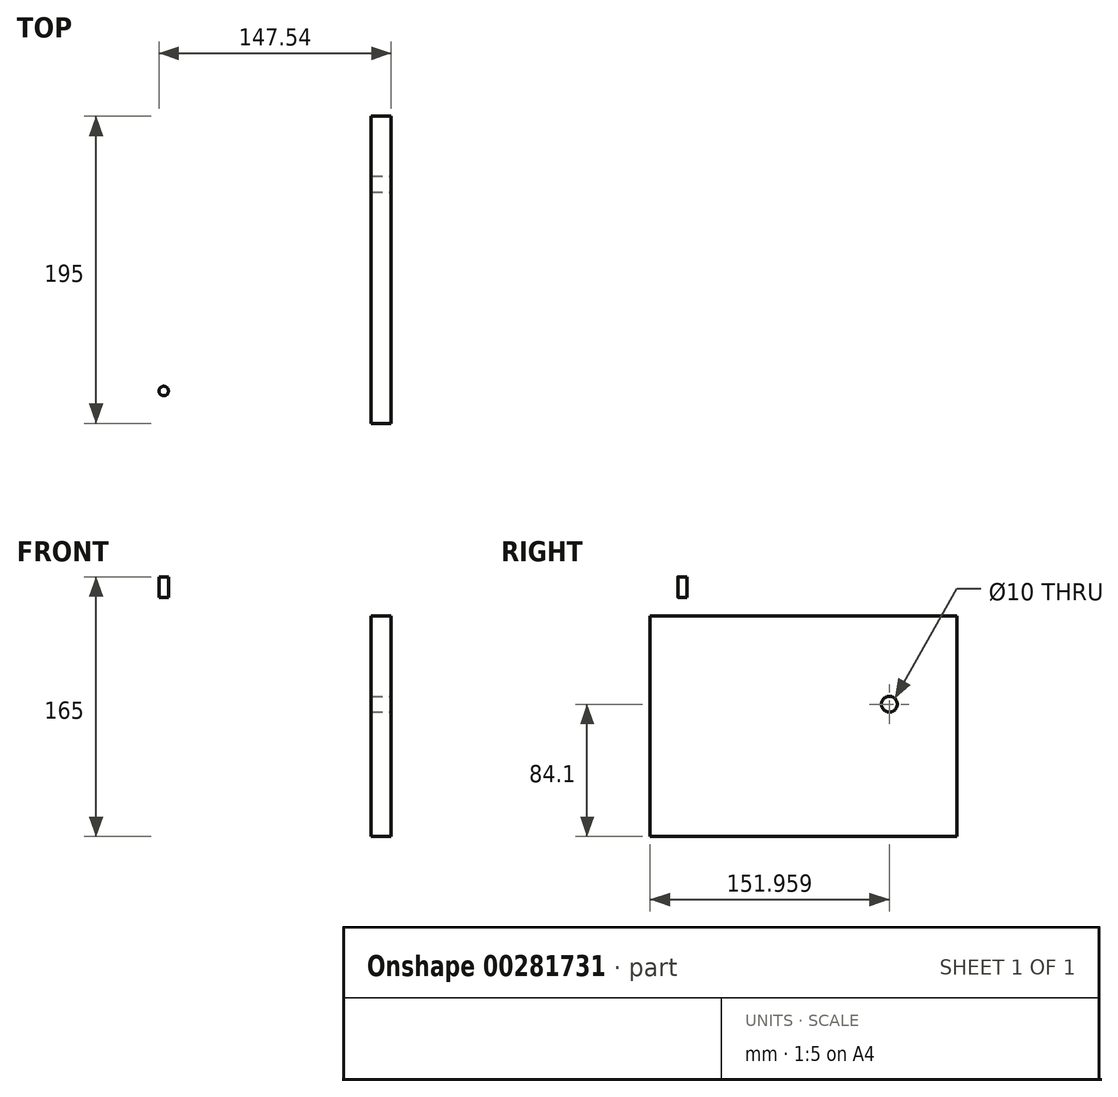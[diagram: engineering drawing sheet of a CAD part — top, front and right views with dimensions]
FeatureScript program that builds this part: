
annotation { "Feature Type Name" : "Feature", "Feature Type Description" : "" }
export const myFeature = defineFeature(function(context is Context, id is Id, definition is map)
    precondition{}
    {
        {
            var Q0;
            Q0=qCreatedBy(makeId("Front.planeOp"),FACE);
            var sketch = newSketch(context, id + "F0", { "sketchPlane" : qUnion([Q0])});
            skLineSegment(sketch, "E0", {"start": v(-1.16, 80.9) * mm, "end": v(-1.16, -84.1) * mm});
            skLineSegment(sketch, "E1", {"start": v(-1.16, -84.1) * mm, "end": v(-14.16, -84.1) * mm});
            skLineSegment(sketch, "E2", {"start": v(-14.16, -84.1) * mm, "end": v(-14.16, 57.9) * mm});
            skLineSegment(sketch, "E3", {"start": v(-24.16, 67.9) * mm, "end": v(-166.16, 67.9) * mm});
            skLineSegment(sketch, "E4", {"start": v(-166.16, 67.9) * mm, "end": v(-166.16, 80.9) * mm});
            skLineSegment(sketch, "E5", {"start": v(-166.16, 80.9) * mm, "end": v(-1.16, 80.9) * mm});
            skPoint(sketch, "E6.visualSharp", {"position": v(-14.16, 67.9) * mm});
            skArc(sketch, "E6.filletArc", {"start": v(-14.16, 57.9) * mm, "mid": v(-17.09, 64.97) * mm, "end": v(-24.16, 67.9) * mm});
            skSolve(sketch);
        }
        {
            var Q0;
            Q0=makeQuery(id+"F0.imprint","IMPRINT",FACE,{"disambiguationData":[TD([[makeQuery(id+"F0.imprint","IMPRINT",EDGE,{"derivedFrom":sQuery(id+"F0.wireOp",EDGE,"E0")}),-1.0]])]});
            extrude(context, id + "F1", {"entities" : qUnion([Q0]), "depth" : 195 * mm});
        }
        {
            var Q0;
            Q0=makeQuery(id+"F1.opExtrude","SWEPT_FACE",FACE,{"disambiguationData":[OSD([sQuery(id+"F0.wireOp",EDGE,"E5")])]});
            var sketch = newSketch(context, id + "F2", { "sketchPlane" : qUnion([Q0])});
            skCircle(sketch, "E7.MirrorC", {"center": v(-145.7, -174.46) * mm, "radius": 3 * mm});
            skArc(sketch, "E8.MirrorCS", {"start": v(-49.52, -16.1) * mm, "mid": v(-53.64, -17.1) * mm, "end": v(-52.63, -21.23) * mm});
            skArc(sketch, "E9.MirrorCS", {"start": v(-49.52, -16.1) * mm, "mid": v(-53.64, -17.1) * mm, "end": v(-52.63, -21.23) * mm, "construction": true});
            skArc(sketch, "E10.MirrorCS", {"start": v(-42.17, -28.1) * mm, "mid": v(-38, -27.38) * mm, "end": v(-38.7, -23.2) * mm});
            skArc(sketch, "E11.MirrorCS", {"start": v(-52.63, -21.23) * mm, "mid": v(-47.34, -24.57) * mm, "end": v(-42.17, -28.1) * mm});
            skArc(sketch, "E12.MirrorCS", {"start": v(-52.63, -21.23) * mm, "mid": v(-47.34, -24.57) * mm, "end": v(-42.17, -28.1) * mm, "construction": true});
            skArc(sketch, "E13.MirrorCS", {"start": v(-42.17, -28.1) * mm, "mid": v(-38, -27.38) * mm, "end": v(-38.7, -23.2) * mm, "construction": true});
            skArc(sketch, "E14.MirrorCS", {"start": v(-51.08, -18.67) * mm, "mid": v(-45.7, -22.06) * mm, "end": v(-40.44, -25.65) * mm, "construction": true});
            skArc(sketch, "E15.MirrorCS", {"start": v(-49.52, -16.1) * mm, "mid": v(-44.05, -19.56) * mm, "end": v(-38.7, -23.2) * mm});
            skArc(sketch, "E16.MirrorCS", {"start": v(-49.52, -16.1) * mm, "mid": v(-44.05, -19.56) * mm, "end": v(-38.7, -23.2) * mm, "construction": true});
            skArc(sketch, "E17.MirrorCS", {"start": v(-140.48, -25.15) * mm, "mid": v(-137.38, -22.26) * mm, "end": v(-140.27, -19.16) * mm});
            skArc(sketch, "E18.MirrorCS", {"start": v(-151.12, -19.16) * mm, "mid": v(-154.01, -22.26) * mm, "end": v(-150.91, -25.15) * mm});
            skArc(sketch, "E19.MirrorCS", {"start": v(-151.02, -22.16) * mm, "mid": v(-145.7, -22.06) * mm, "end": v(-140.38, -22.16) * mm, "construction": true});
            skArc(sketch, "E20.MirrorCS", {"start": v(-150.91, -25.15) * mm, "mid": v(-145.7, -25.06) * mm, "end": v(-140.48, -25.15) * mm});
            skArc(sketch, "E21.MirrorCS", {"start": v(-151.12, -19.16) * mm, "mid": v(-145.7, -19.06) * mm, "end": v(-140.27, -19.16) * mm});
            skSolve(sketch);
        }
        {
            var Q0;
            Q0=makeQuery(id+"F2.imprint","IMPRINT",FACE,{"disambiguationData":[TD([[makeQuery(id+"F2.imprint","IMPRINT",EDGE,{"derivedFrom":sQuery(id+"F2.wireOp",EDGE,"E17.MirrorCS")}),1.0]])]});
            var Q1;
            Q1=makeQuery(id+"F2.imprint","IMPRINT",FACE,{"disambiguationData":[TD([[makeQuery(id+"F2.imprint","IMPRINT",EDGE,{"derivedFrom":sQuery(id+"F2.wireOp",EDGE,"E8.MirrorCS")}),1.0]])]});
            var Q2;
            Q2=makeQuery(id+"F2.imprint","IMPRINT",FACE,{"disambiguationData":[TD([[makeQuery(id+"F2.imprint","IMPRINT",EDGE,{"derivedFrom":sQuery(id+"F2.wireOp",EDGE,"E7.MirrorC")}),-1.0]])]});
            extrude(context, id + "F3", {"entities" : qUnion([Q0, Q1, Q2]), "operationType" : NewBodyOperationType.REMOVE, "oppositeDirection" : true, "depth" : 25 * mm});
        }
        {
            var Q0;
            Q0=makeQuery(id+"F1.opExtrude","SWEPT_FACE",FACE,{"disambiguationData":[OSD([sQuery(id+"F0.wireOp",EDGE,"E0")])]});
            var sketch = newSketch(context, id + "F4", { "sketchPlane" : qUnion([Q0])});
            skCircle(sketch, "E22", {"center": v(-43.04, 0) * mm, "radius": 5 * mm});
            skSolve(sketch);
        }
        {
            var Q0;
            Q0=makeQuery(id+"F4.imprint","IMPRINT",FACE,{"disambiguationData":[TD([[makeQuery(id+"F4.imprint","IMPRINT",EDGE,{"derivedFrom":sQuery(id+"F4.wireOp",EDGE,"E22")}),1.0]])]});
            extrude(context, id + "F5", {"entities" : qUnion([Q0]), "operationType" : NewBodyOperationType.REMOVE, "oppositeDirection" : true, "depth" : 25 * mm, "offsetDistance" : 25 * mm});
        }
    });
